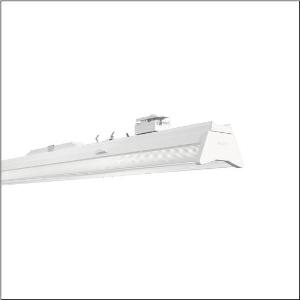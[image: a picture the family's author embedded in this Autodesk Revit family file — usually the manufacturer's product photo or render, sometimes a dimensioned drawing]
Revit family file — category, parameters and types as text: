
# Revit family: licross_r__21_performance_mo_52tm16cn46xg_6fd6
name_source: partatom
category: Lighting Fixtures
units: mm (PartAtom-declared; Revit-internal decimal feet)

## family parameters
Cut with Voids When Loaded = No
Host = Face
Light Source = No
Part Type = Normal
Room Calculation Point = No
Round Connector Dimension = Use Diameter
Shared = No

## types (1)
- --- (1 x LED, 6000 lm, 32 W, 4000K)
    Apparent Load = 32 VA
    CIE Flux Codes = 66 88 96 79 100
    Color Rendering = 80
    Color Temperature = 4000K
    Default Elevation = 1800 mm
    Description = Licross® 21 Performance MO, luminaire insert, of sheet steel, galvanised, coil coated, white, length: 1.500mm, width: 120mm, height: 123mm, LED rated luminous flux: 6.000lm, light colour: 840, SDCM (Standard Deviation of Colour Matching)MacAdam ≤ 3 SDCM (initial), control gear: ON/OFF Multilumen, CLOi, with plug, 3-pole, with phase selection, mains connection: 220..240V, AC, 50/60Hz, start of lifetime: 32W, end of service life: 38W, internal wiring halogen-free, primary light control with lens, of plastic, primary optical cover: cover, of PMMA, light emission: direct/indirect distribution, primary light characteristic: symmetric, protection rating (complete): IP40, insulation class (complete): insulation class I (protective earthing), certification: CE, ENEC, UKCA, protection symbol: D if used in an environment without relevant dust loads with corresponding accessories, impact resistance: IK06, permissible ambient temperature for indoor applications: -35..+55°C, corresponds to IFS (International Featured Standards) requirements for safety and quality in the food industry, reducing of maximum allowable ambient temperature of 5°C with ceiling mounting, LABS conformity tested according to VDMA 24364:2018-05, packaging unit: 1 piece
    Height = 114 mm
    Lamp = 1 x LED
    Lamp Light Flux = 6000 lm
    Lamp Power = 32 W
    Lamp count = 1
    Length = 1500 mm
    Luminous efficacy = 188 lm/W
    Manufacturer = Siteco
    ModVariant = No
    Model = 52TM16CN46XG
    Mounting Place = Ceiling
    Mounting Type = Pendant
    Number of Poles = 1
    OnlyDefault = Yes
    Power Factor = 1
    Product Name = Licross® 21 Performance MO
    Product group = luminaire insert | ceiling pendant
    ProductGroupID = 901
    Protection Class = Protection class I
    Protection Degree = IP 40
    RLX_Detail_Level = 1
    RLX_Emergency_Light_Flux = 0 lm
    RLX_Emergency_Type = 0
    RLX_Emergency_Type_DB = No
    RlxData = <blob elided: 31957 chars, md5=63acedfa>
    Socket = socket
    Standby Power = 0 W
    System Light Flux = 6000 lm
    System Power = 32 W
    Type Comments = factory setting: luminous flux: 100 % | (A | C | E) | 74 mA
    Type Image = l_1256138.jpg
    URL = http://relux.com
    VarID = @adj_115487
    Voltage = 0 V
    Weight = 0.00 kg
    Width = 120 mm

## geometry (parser evidence)
native form markers: Blend x4, Sweep x10
no freeform markers — native parametric forms only
